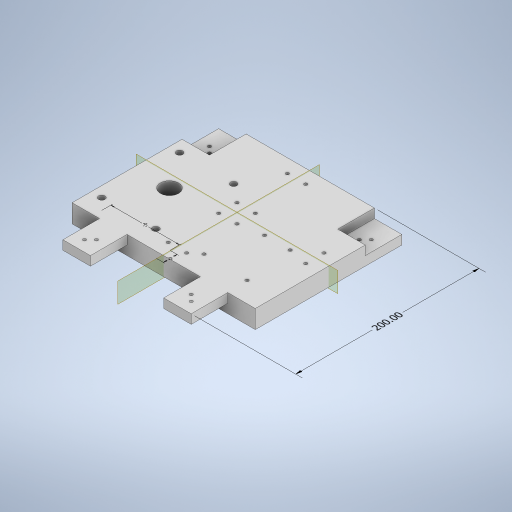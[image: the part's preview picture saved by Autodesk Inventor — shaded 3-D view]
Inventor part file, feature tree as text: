
AUTODESK INVENTOR PART (.ipt)
format: ipt  version: 2023 (Build 270158000, 158)  size: 447,488 bytes
history: native  units: mm
features: sketch x11, extrude x5, hole x5, other x3, plane x2
ambient origin geometry x8: Origin, YZ Plane, XZ Plane, XY Plane, X Axis, Y Axis, Z Axis, Center Point
bodies: Body1 (feature_tree)
feature tree (26):
  other  "Sólido1"
  other  "Anotaciones"
  extrude  "Extrusión1"  Depth=160.0mm
  extrude  "Extrusión2"  Depth=30.0mm
  hole  "Agujero1"  [1 undecoded]
  extrude  "Extrusión3"  Depth=11.75mm
  hole  "Agujero2"  [1 undecoded]
  hole  "Agujero3"  [1 undecoded]
  extrude  "Extrusión4"  TaperAngle=0.0deg  [1 undecoded]
  plane  "Plano de trabajo1"
  plane  "Plano de trabajo2"
  hole  "Agujero4"  [1 undecoded]
  hole  "Agujero5"  [1 undecoded]
  extrude  "Extrusión5"  Depth=200.0mm
  sketch  "Boceto11"  dims[d52=3.5mm d53=6.0mm d54=4.0mm d55=2.0mm d56=90.0deg d57=8.0mm d58=20.594885mm d59=7.0mm d60=7.0mm d61=7.0mm d62=39.0mm d63=46.0mm d64=59.0mm d65=46.0mm d66=39.0mm d67=59.0mm d68=52.0mm d69=70.0mm d70=22.0mm d71=42.0mm d72=3.5mm d73=3.5mm d74=3.5mm d75=3.5mm d76=3.5mm d77=6.0mm d78=4.0mm d79=2.0mm d80=90.0deg d81=8.0mm d82=20.594885mm d83=7.0mm d84=7.0mm d85=7.0mm d86=39.0mm d87=46.0mm d88=59.0mm d89=46.0mm d90=39.0mm d91=59.0mm d92=20.0mm d93=0.0mm d97=40.000127mm d98=10.0mm d99=30.0mm d100=10.0mm d101=5.0mm d102=5.0mm d103=5.0mm d104=5.0mm d105=45.0deg d106=45.0deg d107=10.0mm d108=10.0mm d109=30.0mm d110=5.0mm d111=5.0mm d112=5.0mm d113=5.0mm d114=10.0mm d115=30.0mm d116=5.0mm d117=5.0mm d118=5.0mm d119=5.0mm d120=10.0mm d121=3.5mm d122=6.0mm d123=4.0mm d124=2.0mm d125=90.0deg d126=8.0mm d127=20.594885mm d128=3.5mm d129=10.0mm d130=10.0mm d131=3.5mm d132=6.0mm d133=4.0mm d134=2.0mm d135=90.0deg d136=8.0mm d137=20.594885mm d138=32.0mm d139=32.0mm d140=10.0mm d141=0.0mm d142=17.37633mm d143=12.709242mm d144=6.683722mm d145=12.708891mm d146=5.220756mm d147=1.603663mm d148=2.153068mm d149=6.490327mm d150=75.0mm d151=15.0mm d94=6.100674mm d95=2.550465mm d96=200.0mm]
  sketch  "Boceto1"  dims[d0=200.0mm d1=160.0mm]
  sketch  "Boceto2"  dims[d2=20.0mm d3=0.0mm d4=30.0mm]
  sketch  "Boceto3"  dims[d5=40.0mm d6=10.0mm d7=0.0mm]
  sketch  "Boceto4"  dims[d23=21.75mm d24=11.75mm]
  sketch  "Boceto5"  dims[d26=11.75mm]
  sketch  "Boceto6"  dims[d27=3.5mm d28=6.0mm d29=4.0mm d30=2.0mm d31=90.0deg d32=8.0mm d33=20.594885mm d34=30.0mm]
  sketch  "Boceto7"  dims[d35=10.0mm d36=30.0mm]
  sketch  "Boceto8"  dims[d37=40.0mm d38=0.0mm]
  sketch  "Boceto9"  dims[d39=10.0mm d40=10.0mm d41=40.0mm d42=0.0mm d43=6.5mm d44=6.5mm d45=3.5mm d46=3.5mm d47=11.749873mm d48=11.75mm d49=0.0mm]
  sketch  "Boceto10"  dims[d50=11.75mm d51=0.0mm]
  other  "Cota lineal 1"
note: 6 required parameter values undecoded (feature->parameter linkage not recoverable at this tier; creation-order binding heuristic only, values carry confidence <= 0.55)
